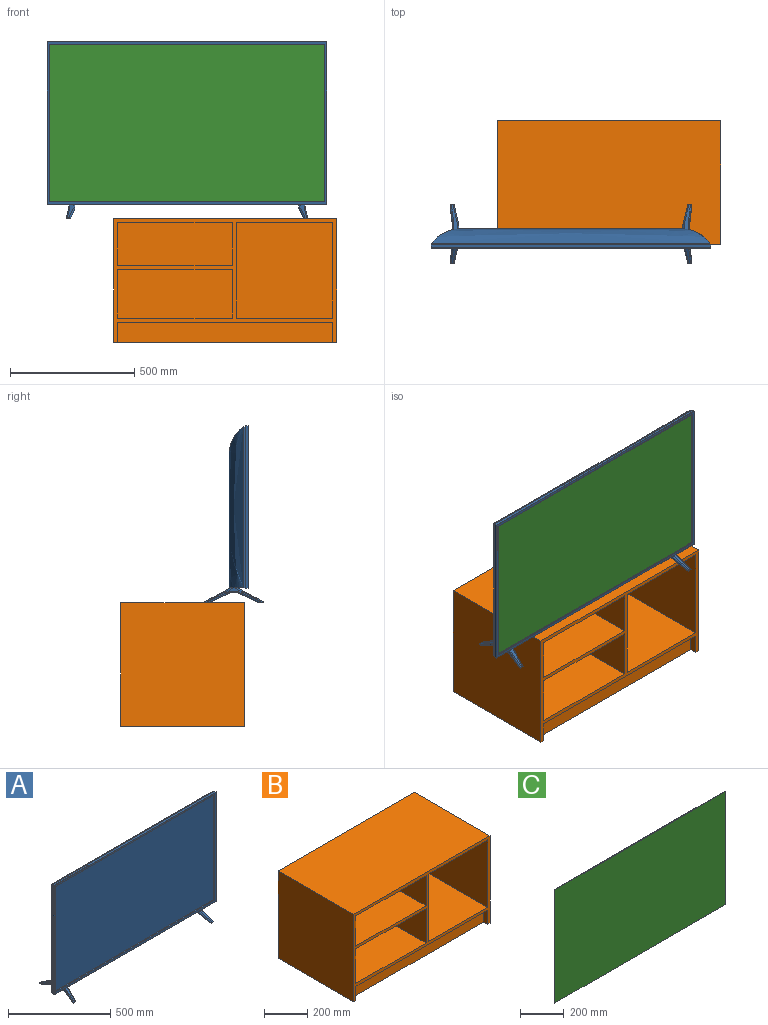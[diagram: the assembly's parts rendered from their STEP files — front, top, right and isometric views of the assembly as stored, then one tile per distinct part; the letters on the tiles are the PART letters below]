
ASSEMBLY  parts=3 mates=2
PART A: 157 faces, bbox 1129x244.2x722.1 mm
  f0: plane 1121.56x67.46mm, normal (0,0,-1), area 65975mm2, adj f1,f12,f13,f14,f16,f17,f44,f47
  f1: plane 1122.93x653.03mm, normal (0,1,0), area 9444.6mm2, adj f0,f15,f16,f17,f26,f27,f36,f37
  f2: plane 653.03x11.68mm, normal (-1,0,0), area 7630mm2, adj f28,f37,f38,f42
  f3: plane 1122.93x11.68mm, normal (0,0,-1), area 13120.4mm2, adj f31,f36,f39,f42
  f4: plane 653.03x11.68mm, normal (1,0,0), area 7630mm2, adj f23,f26,f30,f31
  f5: plane 1122.93x11.68mm, normal (0,0,1), area 13120.4mm2, adj f23,f27,f28,f29
  f6: plane 1122.93x653.03mm, normal (0,-1,0), area 35454.4mm2, adj f19,f20,f21,f22,f29,f30,f38,f39
  f7: plane 631.83x6.35mm, normal (1,0,0), area 4012.1mm2, adj f8,f10,f11,f19
  f8: plane 1101.73x6.35mm, normal (0,0,1), area 6996mm2, adj f7,f9,f11,f21
  f9: plane 631.83x6.35mm, normal (-1,0,0), area 4012.1mm2, adj f8,f10,f11,f22
  f10: plane 1101.73x6.35mm, normal (0,0,-1), area 6996mm2, adj f7,f9,f11,f20
  f11: plane 1101.73x631.83mm, normal (0,-1,0), area 696097.4mm2, adj f7,f8,f9,f10
  f12: extruded ~647.7x101.6mm, area 71889.5mm2, adj f0,f14,f16,f18
  f13: extruded ~647.7x101.6mm, area 71889.5mm2, adj f0,f14,f17,f18
  f14: plane 914.4x546.1mm, normal (0,1,0), area 499353.8mm2, adj f0,f12,f13,f18
  f15: plane 1117.6x6.35mm, normal (0,0,1), area 7096.8mm2, adj f1,f16,f17,f18
  f16: plane 647.7x6.35mm, normal (-1,0,0), area 4112.9mm2, adj f0,f1,f12,f15
  f17: plane 647.7x6.35mm, normal (1,0,0), area 4112.9mm2, adj f0,f1,f13,f15
  f18: extruded ~1117.6x101.6mm, area 122386.5mm2, adj f12,f13,f14,f15
  f19: cylinder r=0.51mm len=632.84mm, axis (0,0,1), area 504.6mm2, adj f6,f7,f20,f21
  f20: cylinder r=0.51mm len=1102.74mm, axis (1,0,0), area 879.5mm2, adj f6,f10,f19,f22
  f21: cylinder r=0.51mm len=1102.74mm, axis (-1,0,0), area 879.5mm2, adj f6,f8,f19,f22
  f22: cylinder r=0.51mm len=632.84mm, axis (0,0,-1), area 504.6mm2, adj f6,f9,f20,f21
  f23: cylinder r=0.51mm len=11.68mm, axis (0,-1,0), area 9.3mm2, adj f4,f5,f24,f25
  f24: sphere r=0.51mm, area 0.3mm2, adj f23,f26,f27
  f25: sphere r=0.51mm, area 0.4mm2, adj f23,f29,f30
  f26: cylinder r=0.51mm len=653.03mm, axis (0,0,-1), area 521.1mm2, adj f1,f4,f24,f32
  f27: cylinder r=0.51mm len=1122.93mm, axis (1,0,0), area 896.1mm2, adj f1,f5,f24,f33
  f28: cylinder r=0.51mm len=11.68mm, axis (0,1,0), area 9.3mm2, adj f2,f5,f33,f34
  f29: cylinder r=0.51mm len=1122.93mm, axis (-1,0,0), area 896.1mm2, adj f5,f6,f25,f34
  f30: cylinder r=0.51mm len=653.03mm, axis (0,0,1), area 521.1mm2, adj f4,f6,f25,f35
  f31: cylinder r=0.51mm len=11.68mm, axis (0,1,0), area 9.3mm2, adj f3,f4,f32,f35
  f32: sphere r=0.51mm, area 0.3mm2, adj f26,f31,f36
  f33: sphere r=0.51mm, area 0.6mm2, adj f27,f28,f37
  f34: sphere r=0.51mm, area 0.3mm2, adj f28,f29,f38
  f35: sphere r=0.51mm, area 0.6mm2, adj f30,f31,f39
  f36: cylinder r=0.51mm len=1122.93mm, axis (-1,0,0), area 896.1mm2, adj f1,f3,f32,f40
  f37: cylinder r=0.51mm len=653.03mm, axis (0,0,1), area 521.1mm2, adj f1,f2,f33,f40
  f38: cylinder r=0.51mm len=653.03mm, axis (0,0,-1), area 521.1mm2, adj f2,f6,f34,f41
  f39: cylinder r=0.51mm len=1122.93mm, axis (1,0,0), area 896.1mm2, adj f3,f6,f35,f41
  f40: sphere r=0.51mm, area 0.6mm2, adj f36,f37,f42
  f41: sphere r=0.51mm, area 0.4mm2, adj f38,f39,f42
  f42: cylinder r=0.51mm len=11.68mm, axis (0,-1,0), area 9.3mm2, adj f2,f3,f40,f41
  f43: cylinder r=5.08mm len=14.06mm, axis (0,1,0), area 30.2mm2, adj f44,f54,f70,f85
  f44: plane 72.95x18.59mm, normal (1,0,0), area 571.5mm2, adj f0,f43,f69,f71,f72,f80,f81,f82
  f45: plane 16.92x4.87mm, normal (0,-1,0), area 50.7mm2, adj f49,f52,f65,f66
  f46: plane 87.56x39.65mm, normal (0.91,0,-0.41), area 353.4mm2, adj f49,f63,f65,f71,f78
  f47: plane 74.67x19.06mm, normal (-1,0,0), area 576.7mm2, adj f0,f67,f68,f87,f90,f95,f96,f97
  f48: plane 87.42x40.99mm, normal (-0.97,0,0.24), area 298.4mm2, adj f49,f64,f66,f87,f88,f93
  f49: plane 22.31x22.31mm, normal (0,0,-1), area 267.9mm2, adj f45,f46,f48,f50,f63,f64,f65,f66
  f50: plane 86.49x40.17mm, normal (0,0.42,-0.91), area 1082.4mm2, adj f49,f63,f64,f75,f80
  f51: plane 23.48x15.24mm, normal (0,0,-1), area 353mm2, adj f74,f75,f76,f77,f82,f96
  f52: plane 104.78x56.52mm, normal (0,-0.47,0.88), area 1398.2mm2, adj f0,f45,f65,f66,f68,f72
  f53: plane 16.92x4.87mm, normal (0,1,0), area 50.7mm2, adj f56,f58,f59,f60
  f54: plane 87.77x39.85mm, normal (0.91,0,-0.41), area 353.4mm2, adj f43,f56,f60,f61,f86
  f55: plane 87.42x40.99mm, normal (-0.97,0,0.24), area 298.4mm2, adj f56,f59,f62,f90,f91,f99
  f56: plane 22.31x22.31mm, normal (0,0,-1), area 267.9mm2, adj f53,f54,f55,f57,f59,f60,f61,f62
  f57: plane 86.49x40.17mm, normal (0,-0.42,-0.91), area 1082.4mm2, adj f56,f61,f62,f77,f84
  f58: plane 104.78x56.52mm, normal (0,0.47,0.88), area 1398.2mm2, adj f0,f53,f59,f60,f67,f69
  f59: cylinder r=5.08mm len=79.91mm, axis (0.12,-0.87,0.47), area 600.8mm2, adj f53,f55,f56,f58,f92
  f60: cylinder r=5.08mm len=81.89mm, axis (-0.21,0.86,-0.46), area 893.3mm2, adj f53,f54,f56,f58,f70
  f61: cylinder r=5.08mm len=87.5mm, axis (0.19,-0.89,0.41), area 557.2mm2, adj f54,f56,f57,f85,f86
  f62: cylinder r=5.08mm len=101.25mm, axis (-0.1,0.9,-0.42), area 827.1mm2, adj f55,f56,f57,f76,f99
  f63: cylinder r=5.08mm len=87.5mm, axis (0.19,0.89,0.41), area 557.2mm2, adj f46,f49,f50,f78,f79
  f64: cylinder r=5.08mm len=101.25mm, axis (-0.1,-0.9,-0.42), area 827.1mm2, adj f48,f49,f50,f74,f93
  f65: cylinder r=5.08mm len=81.89mm, axis (-0.21,-0.86,-0.46), area 893.3mm2, adj f45,f46,f49,f52,f73
  f66: cylinder r=5.08mm len=79.91mm, axis (0.12,0.87,0.47), area 600.8mm2, adj f45,f48,f49,f52,f89
  f67: cylinder r=5.08mm len=40.07mm, axis (0,-0.88,0.47), area 289.8mm2, adj f0,f47,f58,f91,f92
  f68: cylinder r=5.08mm len=40.07mm, axis (0,0.88,0.47), area 289.8mm2, adj f0,f47,f52,f88,f89
  f69: cylinder r=5.08mm len=36.89mm, axis (0,-0.88,0.47), area 275mm2, adj f0,f44,f58,f70
  f70: sphere r=5.08mm, area 6.5mm2, adj f43,f60,f69
  f71: cylinder r=5.08mm len=14.06mm, axis (0,1,0), area 30.2mm2, adj f44,f46,f73,f79
  f72: cylinder r=5.08mm len=36.89mm, axis (0,0.88,0.47), area 275mm2, adj f0,f44,f52,f73
  f73: sphere r=5.08mm, area 6.5mm2, adj f65,f71,f72
  f74: bspline ~15.85x10.77mm, area 9.6mm2, adj f51,f64,f75,f94,f95
  f75: cylinder r=5.08mm len=14.05mm, axis (1,0,0), area 31mm2, adj f50,f51,f74,f81
  f76: bspline ~15.85x10.77mm, area 9.6mm2, adj f51,f62,f77,f97,f98
  f77: cylinder r=5.08mm len=14.05mm, axis (1,0,0), area 31mm2, adj f51,f57,f76,f83
  f78: bspline ~6.12x2.49mm, area 2.1mm2, adj f46,f63,f79
  f79: sphere r=5.08mm, area 3.9mm2, adj f63,f71,f78,f80
  f80: cylinder r=5.08mm len=8.69mm, axis (0,-0.91,-0.42), area 57.7mm2, adj f44,f50,f79,f81
  f81: torus R=10.16mm, axis (1,0,0), area 24mm2, adj f44,f75,f80,f82
  f82: cylinder r=5.08mm len=23.16mm, axis (0,1,0), area 184.8mm2, adj f44,f51,f81,f83
  f83: torus R=10.16mm, axis (1,0,0), area 24mm2, adj f44,f77,f82,f84
  f84: cylinder r=5.08mm len=8.69mm, axis (0,-0.91,0.42), area 57.7mm2, adj f44,f57,f83,f85
  f85: sphere r=5.08mm, area 4.3mm2, adj f43,f61,f84,f86
  f86: bspline ~5.45x2.22mm, area 2.1mm2, adj f54,f61,f85
  f87: cylinder r=5.08mm len=13.22mm, axis (0,-1,0), area 13.6mm2, adj f47,f48,f88,f94
  f88: bspline ~2.83x1.23mm, area 2.5mm2, adj f48,f68,f87,f89
  f89: bspline ~5.05x3.75mm, area 1.5mm2, adj f66,f68,f88
  f90: cylinder r=5.08mm len=13.22mm, axis (0,1,0), area 13.6mm2, adj f47,f55,f91,f98
  f91: bspline ~3.97x1.73mm, area 2.5mm2, adj f55,f67,f90,f92
  f92: bspline ~5.05x3.75mm, area 1.5mm2, adj f59,f67,f91
  f93: bspline ~16.26x6.85mm, area 14.4mm2, adj f48,f64,f94
  f94: bspline ~11.26x5.24mm, area 16.2mm2, adj f74,f87,f93,f95
  f95: bspline ~13.78x7.44mm, area 68.1mm2, adj f47,f74,f94,f96
  f96: cylinder r=5.08mm len=23.48mm, axis (0,-1,0), area 187.3mm2, adj f47,f51,f95,f97
  f97: bspline ~14.81x7.59mm, area 68.1mm2, adj f47,f76,f96,f98
  f98: bspline ~12.34x5.54mm, area 16.2mm2, adj f76,f90,f97,f99
  f99: bspline ~16.91x7.12mm, area 14.5mm2, adj f55,f62,f98
  f100: cylinder r=5.08mm len=14.06mm, axis (0,1,0), area 30.2mm2, adj f101,f111,f127,f142
  f101: plane 72.95x18.59mm, normal (-1,0,0), area 571.5mm2, adj f0,f100,f126,f128,f129,f137,f138,f139
  f102: plane 16.92x4.87mm, normal (0,-1,0), area 50.7mm2, adj f106,f109,f122,f123
  f103: plane 88.2x40.28mm, normal (-0.91,0,-0.41), area 353.4mm2, adj f106,f120,f122,f128,f135
  f104: plane 74.67x19.06mm, normal (1,0,0), area 576.7mm2, adj f0,f124,f125,f144,f147,f152,f153,f154
  f105: plane 87.42x40.99mm, normal (0.97,0,0.24), area 298.4mm2, adj f106,f121,f123,f144,f145,f150
  f106: plane 22.31x22.31mm, normal (0,0,-1), area 267.9mm2, adj f102,f103,f105,f107,f120,f121,f122,f123
  f107: plane 86.49x40.17mm, normal (0,0.42,-0.91), area 1082.4mm2, adj f106,f120,f121,f132,f137
  f108: plane 23.48x15.24mm, normal (0,0,-1), area 353mm2, adj f131,f132,f133,f134,f139,f153
  f109: plane 104.78x56.52mm, normal (0,-0.47,0.88), area 1398.2mm2, adj f0,f102,f122,f123,f125,f129
  f110: plane 16.92x4.87mm, normal (0,1,0), area 50.7mm2, adj f113,f115,f116,f117
  f111: plane 87.84x39.93mm, normal (-0.91,0,-0.41), area 353.4mm2, adj f100,f113,f117,f118,f143
  f112: plane 88.99x42.56mm, normal (0.97,0,0.24), area 298.4mm2, adj f113,f116,f119,f147,f148,f156
  f113: plane 22.31x22.31mm, normal (0,0,-1), area 267.9mm2, adj f110,f111,f112,f114,f116,f117,f118,f119
  f114: plane 86.49x40.17mm, normal (0,-0.42,-0.91), area 1082.4mm2, adj f113,f118,f119,f134,f141
  f115: plane 104.78x56.52mm, normal (0,0.47,0.88), area 1398.2mm2, adj f0,f110,f116,f117,f124,f126
  f116: cylinder r=5.08mm len=79.91mm, axis (-0.12,-0.87,0.47), area 600.8mm2, adj f110,f112,f113,f115,f149
  f117: cylinder r=5.08mm len=81.89mm, axis (0.21,0.86,-0.46), area 893.3mm2, adj f110,f111,f113,f115,f127
  f118: cylinder r=5.08mm len=87.5mm, axis (-0.19,-0.89,0.41), area 557.2mm2, adj f111,f113,f114,f142,f143
  f119: cylinder r=5.08mm len=101.25mm, axis (0.1,0.9,-0.42), area 827.1mm2, adj f112,f113,f114,f133,f156
  f120: cylinder r=5.08mm len=87.5mm, axis (-0.19,0.89,0.41), area 557.2mm2, adj f103,f106,f107,f135,f136
  f121: cylinder r=5.08mm len=101.25mm, axis (0.1,-0.9,-0.42), area 827.1mm2, adj f105,f106,f107,f131,f150
  f122: cylinder r=5.08mm len=81.89mm, axis (0.21,-0.86,-0.46), area 893.3mm2, adj f102,f103,f106,f109,f130
  f123: cylinder r=5.08mm len=79.91mm, axis (-0.12,0.87,0.47), area 600.8mm2, adj f102,f105,f106,f109,f146
  f124: cylinder r=5.08mm len=40.07mm, axis (0,-0.88,0.47), area 289.8mm2, adj f0,f104,f115,f148,f149
  f125: cylinder r=5.08mm len=40.07mm, axis (0,0.88,0.47), area 289.8mm2, adj f0,f104,f109,f145,f146
  f126: cylinder r=5.08mm len=36.89mm, axis (0,-0.88,0.47), area 275mm2, adj f0,f101,f115,f127
  f127: sphere r=5.08mm, area 6.5mm2, adj f100,f117,f126
  f128: cylinder r=5.08mm len=14.06mm, axis (0,1,0), area 30.2mm2, adj f101,f103,f130,f136
  f129: cylinder r=5.08mm len=36.89mm, axis (0,0.88,0.47), area 275mm2, adj f0,f101,f109,f130
  f130: sphere r=5.08mm, area 6.5mm2, adj f122,f128,f129
  f131: bspline ~15.85x10.77mm, area 9.6mm2, adj f108,f121,f132,f151,f152
  f132: cylinder r=5.08mm len=14.05mm, axis (-1,0,0), area 31mm2, adj f107,f108,f131,f138
  f133: bspline ~15.85x10.77mm, area 9.6mm2, adj f108,f119,f134,f154,f155
  f134: cylinder r=5.08mm len=14.05mm, axis (-1,0,0), area 31mm2, adj f108,f114,f133,f140
  f135: bspline ~4.91x2mm, area 2.1mm2, adj f103,f120,f136
  f136: sphere r=5.08mm, area 3.9mm2, adj f120,f128,f135,f137
  f137: cylinder r=5.08mm len=8.69mm, axis (0,-0.91,-0.42), area 57.7mm2, adj f101,f107,f136,f138
  f138: torus R=10.16mm, axis (-1,0,0), area 24mm2, adj f101,f132,f137,f139
  f139: cylinder r=5.08mm len=23.16mm, axis (0,1,0), area 184.8mm2, adj f101,f108,f138,f140
  f140: torus R=10.16mm, axis (-1,0,0), area 24mm2, adj f101,f134,f139,f141
  f141: cylinder r=5.08mm len=8.69mm, axis (0,-0.91,0.42), area 57.7mm2, adj f101,f114,f140,f142
  f142: sphere r=5.08mm, area 4.3mm2, adj f100,f118,f141,f143
  f143: bspline ~7.08x2.87mm, area 2.1mm2, adj f111,f118,f142
  f144: cylinder r=5.08mm len=13.22mm, axis (0,-1,0), area 13.6mm2, adj f104,f105,f145,f151
  f145: bspline ~2.83x1.23mm, area 2.5mm2, adj f105,f125,f144,f146
  f146: bspline ~5.05x3.75mm, area 1.5mm2, adj f123,f125,f145
  f147: cylinder r=5.08mm len=13.22mm, axis (0,1,0), area 13.6mm2, adj f104,f112,f148,f155
  f148: bspline ~6.15x2.1mm, area 2.5mm2, adj f112,f124,f147,f149
  f149: bspline ~5.05x3.75mm, area 1.5mm2, adj f116,f124,f148
  f150: bspline ~16.26x6.85mm, area 14.4mm2, adj f105,f121,f151
  f151: bspline ~11.26x5.24mm, area 16.2mm2, adj f131,f144,f150,f152
  f152: bspline ~13.78x7.44mm, area 68.1mm2, adj f104,f131,f151,f153
  f153: cylinder r=5.08mm len=23.48mm, axis (0,-1,0), area 187.3mm2, adj f104,f108,f152,f154
  f154: bspline ~15.02x7.65mm, area 68.1mm2, adj f104,f133,f153,f155
  f155: bspline ~12.34x5.54mm, area 16.2mm2, adj f133,f147,f154,f156
  f156: bspline ~16.91x7.12mm, area 14.5mm2, adj f112,f119,f155
PART B: 30 faces, bbox 896.9x496.9x496.9 mm
  f0: plane 81.28x27.94mm, normal (1,0,0), area 2271mm2, adj f1,f14,f23,f25
  f1: plane 865.19x27.94mm, normal (0,0,-1), area 24173.3mm2, adj f0,f2,f23,f25
  f2: plane 81.28x27.94mm, normal (-1,0,0), area 2271mm2, adj f1,f14,f23,f25
  f3: plane 495.3x460.38mm, normal (0,0,1), area 228023.7mm2, adj f4,f21,f23,f27
  f4: plane 495.3x196.53mm, normal (1,0,0), area 97342.5mm2, adj f3,f5,f23,f27
  f5: plane 495.3x460.38mm, normal (0,0,-1), area 228023.7mm2, adj f4,f21,f23,f27
  f6: plane 495.3x171.45mm, normal (1,0,0), area 84919.2mm2, adj f7,f18,f23,f29
  f7: plane 495.3x460.38mm, normal (0,0,-1), area 228023.7mm2, adj f6,f8,f23,f29
  f8: plane 495.3x171.45mm, normal (-1,0,0), area 84919.2mm2, adj f7,f18,f23,f29
  f9: plane 495.3x383.86mm, normal (1,0,0), area 190124.6mm2, adj f10,f19,f23,f28
  f10: plane 495.3x388.94mm, normal (0,0,-1), area 192640.7mm2, adj f9,f11,f23,f28
  f11: plane 495.3x383.86mm, normal (-1,0,0), area 190124.6mm2, adj f10,f19,f23,f28
  f12: plane 896.94x496.89mm, normal (0,0,1), area 445677mm2, adj f13,f20,f22,f23
  f13: plane 496.89x496.89mm, normal (-1,0,0), area 246897.2mm2, adj f12,f14,f22,f23
  f14: plane 896.94x496.89mm, normal (0,0,-1), area 43245.9mm2, adj f0,f2,f13,f15,f17,f20,f22,f23
  f15: plane 437.2x81.28mm, normal (1,0,0), area 35535.4mm2, adj f14,f16,f24,f26
  f16: plane 865.19x437.2mm, normal (0,0,-1), area 378257.8mm2, adj f15,f17,f24,f26
  f17: plane 437.2x81.28mm, normal (-1,0,0), area 35535.4mm2, adj f14,f16,f24,f26
  f18: plane 495.3x460.38mm, normal (0,0,1), area 228023.7mm2, adj f6,f8,f23,f29
  f19: plane 495.3x388.94mm, normal (0,0,1), area 192640.7mm2, adj f9,f11,f23,f28
  f20: plane 496.89x496.89mm, normal (1,0,0), area 246897.2mm2, adj f12,f14,f22,f23
  f21: plane 495.3x196.53mm, normal (-1,0,0), area 97342.5mm2, adj f3,f5,f23,f27
  f22: plane 896.94x496.89mm, normal (0,1,0), area 445677mm2, adj f12,f13,f14,f20
  f23: plane 896.94x496.89mm, normal (0,-1,0), area 56648.1mm2, adj f0,f1,f2,f3,f4,f5,f6,f7
  f24: plane 865.19x81.28mm, normal (0,1,0), area 70322.4mm2, adj f14,f15,f16,f17
  f25: plane 865.19x81.28mm, normal (0,-1,0), area 70322.4mm2, adj f0,f1,f2,f14
  f26: plane 865.19x81.28mm, normal (0,-1,0), area 70322.4mm2, adj f14,f15,f16,f17
  f27: plane 460.38x196.53mm, normal (0,-1,0), area 90478.6mm2, adj f3,f4,f5,f21
  f28: plane 388.94x383.86mm, normal (0,-1,0), area 149296.6mm2, adj f9,f10,f11,f19
  f29: plane 460.38x171.45mm, normal (0,-1,0), area 78931.3mm2, adj f6,f7,f8,f18
PART C: 6 faces, bbox 1101.7x3.4x631.8 mm
  f0: plane 631.83x3.43mm, normal (-1,0,0), area 2166.5mm2, adj f1,f3,f4,f5
  f1: plane 1101.73x3.43mm, normal (0,0,-1), area 3777.8mm2, adj f0,f2,f4,f5
  f2: plane 631.83x3.43mm, normal (1,0,0), area 2166.5mm2, adj f1,f3,f4,f5
  f3: plane 1101.73x3.43mm, normal (0,0,1), area 3777.8mm2, adj f0,f2,f4,f5
  f4: plane 1101.73x631.83mm, normal (0,-1,0), area 696097.4mm2, adj f0,f1,f2,f3
  f5: plane 1101.73x631.83mm, normal (0,1,0), area 696097.4mm2, adj f0,f1,f2,f3
PLACE A t=(-267.41,-15.34,0)mm
PLACE B at identity fixed
PLACE C t=(-267.41,-15.34,0)mm
MATE planar B.f12 <-> A.f106  axis (0,0,1) through (448.47,248.44,0)mm
MATE fastened A.f11 <-> C.f5  axis (0,-1,0) through (294.56,-8.48,384.18)mm
